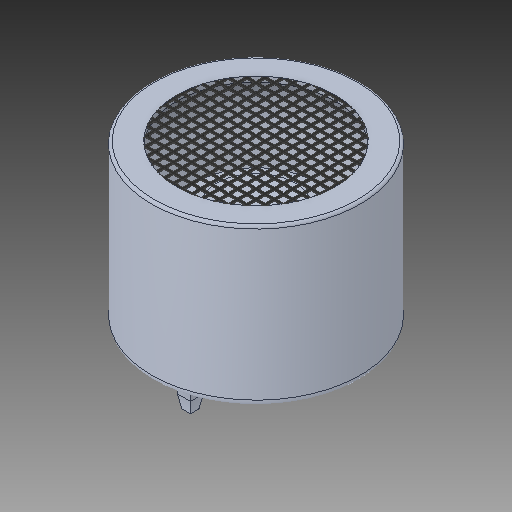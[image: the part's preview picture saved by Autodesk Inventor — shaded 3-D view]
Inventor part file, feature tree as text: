
AUTODESK INVENTOR PART (.ipt)
format: ipt  version: 2018.3 (Build 223284000, 284)  size: 840,192 bytes
history: native  units: mm
features: other x3, chamfer x1
ambient origin geometry x8: Origin, YZ Plane, XZ Plane, XY Plane, X Axis, Y Axis, Z Axis, Center Point
bodies: Body1 (feature_tree), Body2 (feature_tree)
feature tree (4):
  other  "Sólido1"
  other  "Sólido2"
  other  "Boss-Extrude4"
  chamfer  "Chamfer1"  [1 undecoded]
note: 1 required parameter value undecoded (feature->parameter linkage not recoverable at this tier; creation-order binding heuristic only, values carry confidence <= 0.55)
